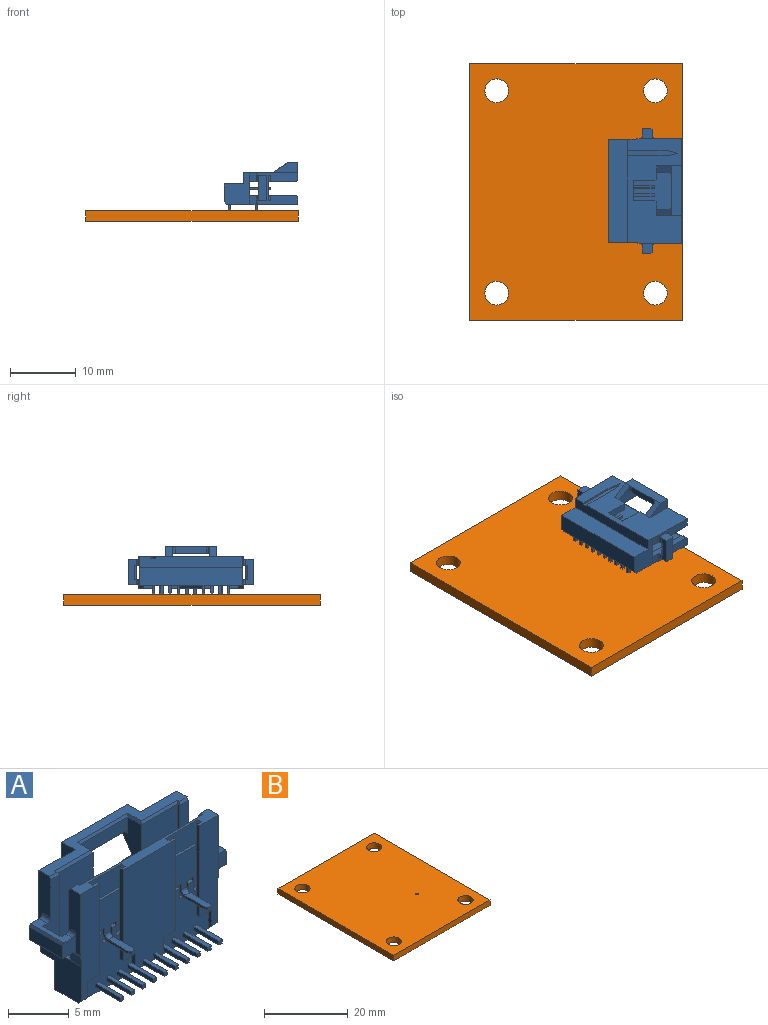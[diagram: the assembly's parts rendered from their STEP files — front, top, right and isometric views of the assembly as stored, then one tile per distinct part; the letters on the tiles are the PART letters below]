
ASSEMBLY  parts=2 mates=1
PART A: 290 faces, bbox 19.1x8.9x11.2 mm
  f0: plane 10.77x2.16mm, normal (0,-1,0), area 20.4mm2, adj f3,f26,f42,f44,f69,f72,f73,f155
  f1: plane 10.77x2.16mm, normal (0,-1,0), area 20.4mm2, adj f26,f28,f60,f62,f68,f70,f131,f132
  f2: plane 10.77x6.1mm, normal (0,-1,0), area 60.9mm2, adj f26,f71,f81,f82,f83,f104,f134,f135
  f3: plane 9.14x0.41mm, normal (1,0,0), area 3.7mm2, adj f0,f4,f15,f24,f26,f73,f74
  f4: plane 4.06x2.79mm, normal (0,-1,0), area 9.6mm2, adj f3,f5,f8,f11,f12,f13,f14,f19
  f5: cylinder r=0.38mm len=0.64mm, axis (1,0,0), area 0.4mm2, adj f4,f6,f8,f112
  f6: plane 2.57x0.64mm, normal (0,0,1), area 1.6mm2, adj f5,f8,f112,f113,f114,f115
  f7: plane 2.57x0.64mm, normal (0,0,1), area 1.6mm2, adj f106,f107,f109,f116,f117,f118
  f8: plane 2.94x1.24mm, normal (1,0,0), area 0.9mm2, adj f4,f5,f6,f9,f10,f11,f110,f115
  f9: cylinder r=0.64mm len=0.64mm, axis (1,0,0), area 0.6mm2, adj f8,f10,f110,f112
  f10: plane 4.06x3.4mm, normal (0,1,0), area 12mm2, adj f8,f9,f11,f12,f13,f14,f17,f18
  f11: plane 0.75x0.25mm, normal (0,0,-1), area 0.2mm2, adj f4,f8,f10,f13
  f12: plane 0.75x0.25mm, normal (0,0,-1), area 0.2mm2, adj f4,f10,f23,f112
  f13: plane 1.02x0.25mm, normal (-1,0,0), area 0.3mm2, adj f4,f10,f11,f14
  f14: plane 0.64x0.25mm, normal (0,0,-1), area 0.2mm2, adj f4,f10,f13,f16,f21
  f15: plane 6.32x0.36mm, normal (0,1,0), area 1mm2, adj f3,f17,f18,f19,f22,f24,f75,f76
  f16: plane 6.32x0.36mm, normal (0,1,0), area 1mm2, adj f14,f19,f20,f21,f80,f81,f84,f85
  f17: plane 3.81x0.25mm, normal (-1,0,0), area 1mm2, adj f10,f15,f18,f22
  f18: cylinder r=0.25mm len=0.25mm, axis (0,1,0), area 0.1mm2, adj f10,f15,f17,f19
  f19: plane 2.9x0.25mm, normal (0,0,1), area 0.7mm2, adj f4,f10,f15,f16,f18,f20
  f20: cylinder r=0.25mm len=0.25mm, axis (0,-1,0), area 0.1mm2, adj f10,f16,f19,f21
  f21: plane 3.81x0.25mm, normal (1,0,0), area 1mm2, adj f10,f14,f16,f20
  f22: plane 0.64x0.25mm, normal (0,0,-1), area 0.2mm2, adj f4,f10,f15,f17,f23
  f23: plane 1.02x0.25mm, normal (1,0,0), area 0.3mm2, adj f4,f10,f12,f22
  f24: plane 0.5x0.25mm, normal (0,0.87,0.5), area 0.1mm2, adj f3,f15,f26,f77
  f25: plane 16x2.72mm, normal (0,0,1), area 17.9mm2, adj f27,f29,f43,f148,f160,f161,f168,f169
  f26: plane 16x1.2mm, normal (0,0,1), area 10.7mm2, adj f0,f1,f2,f3,f24,f28,f35,f36
  f27: plane 1.02x0.25mm, normal (0,-0.87,0.5), area 0.3mm2, adj f25,f29,f55,f173
  f28: plane 6.17x1.35mm, normal (1,0,0), area 6.6mm2, adj f1,f26,f30,f31,f33,f35,f62
  f29: plane 6.17x1.35mm, normal (1,0,0), area 6.3mm2, adj f25,f27,f55,f57,f58,f59,f148
  f30: plane 2.11x1.52mm, normal (0,-1,0), area 2.4mm2, adj f28,f31,f32,f62,f63,f64,f65
  f31: cylinder r=0.38mm len=0.79mm, axis (0,1,0), area 0.5mm2, adj f28,f30,f32,f33
  f32: plane 3.86x1mm, normal (0,0,1), area 2.7mm2, adj f30,f31,f33,f55,f57,f58,f65,f67
  f33: plane 7.11x1.93mm, normal (0,1,0), area 8mm2, adj f28,f31,f32,f35,f37,f60,f62,f63
  f34: plane 7.11x1.93mm, normal (0,1,0), area 8mm2, adj f41,f42,f44,f45,f46,f47,f48,f49
  f35: plane 1.02x0.25mm, normal (0,0.87,0.5), area 0.3mm2, adj f26,f28,f33,f36
  f36: plane 0.4x0.25mm, normal (-0.87,0,0.5), area 0.1mm2, adj f26,f35,f37,f39
  f37: plane 7.11x0.25mm, normal (-1,0,0), area 1.8mm2, adj f33,f36,f38,f147
  f38: plane 13.97x7.11mm, normal (0,1,0), area 99.4mm2, adj f37,f39,f147,f191
  f39: plane 14.26x0.25mm, normal (0,0.87,0.5), area 4.1mm2, adj f26,f36,f38,f40
  f40: plane 0.4x0.25mm, normal (0.87,0,0.5), area 0.1mm2, adj f26,f39,f41,f191
  f41: plane 1.02x0.25mm, normal (0,0.87,0.5), area 0.3mm2, adj f26,f34,f40,f42
  f42: plane 6.17x1.35mm, normal (-1,0,0), area 6.6mm2, adj f0,f26,f34,f41,f44,f49,f50
  f43: plane 6.17x1.35mm, normal (-1,0,0), area 6.3mm2, adj f25,f53,f54,f56,f148,f159,f186
  f44: cylinder r=0.38mm len=1.35mm, axis (0,1,0), area 0.5mm2, adj f0,f34,f42,f45,f50,f157
  f45: plane 3.86x1.19mm, normal (0,0,-1), area 4mm2, adj f34,f44,f46,f50,f51,f53,f56,f159
  f46: cylinder r=0.33mm len=2.13mm, axis (0,1,0), area 1.5mm2, adj f34,f45,f47,f56
  f47: plane 2.13x1.03mm, normal (0.87,0,0.5), area 2.5mm2, adj f34,f46,f48,f56
  f48: plane 3.86x1mm, normal (0,0,1), area 2.7mm2, adj f34,f47,f49,f50,f52,f53,f54,f56
  f49: cylinder r=0.38mm len=0.79mm, axis (0,1,0), area 0.5mm2, adj f34,f42,f48,f50
  f50: plane 2.11x1.52mm, normal (0,-1,0), area 2.4mm2, adj f42,f44,f45,f48,f49,f51,f52
  f51: plane 3.86x1.27mm, normal (-1,0,0), area 4.9mm2, adj f45,f50,f52,f53
  f52: plane 3.86x0.25mm, normal (-0.87,0,0.5), area 1.1mm2, adj f48,f50,f51,f53
  f53: plane 2.11x1.52mm, normal (0,1,0), area 2.4mm2, adj f43,f45,f48,f51,f52,f54,f159
  f54: cylinder r=0.38mm len=0.94mm, axis (0,1,0), area 0.6mm2, adj f43,f48,f53,f56
  f55: plane 7.11x1.93mm, normal (0,-1,0), area 8mm2, adj f27,f29,f32,f57,f59,f61,f63,f66
  f56: plane 7.11x1.93mm, normal (0,-1,0), area 8mm2, adj f43,f45,f46,f47,f48,f54,f147,f158
  f57: cylinder r=0.38mm len=0.94mm, axis (0,1,0), area 0.6mm2, adj f29,f32,f55,f58
  f58: plane 2.11x1.52mm, normal (0,1,0), area 2.4mm2, adj f29,f32,f57,f59,f63,f64,f65
  f59: cylinder r=0.38mm len=1.35mm, axis (0,1,0), area 0.6mm2, adj f29,f55,f58,f61,f63,f148
  f60: plane 1.35x1.06mm, normal (0.99,0,-0.1), area 1.4mm2, adj f1,f33,f62,f68
  f61: plane 1.35x1.06mm, normal (0.99,0,-0.1), area 1.4mm2, adj f55,f59,f68,f148
  f62: cylinder r=0.38mm len=1.35mm, axis (0,1,0), area 0.5mm2, adj f1,f28,f30,f33,f60,f63
  f63: plane 3.86x1.19mm, normal (0,0,-1), area 4mm2, adj f30,f33,f55,f58,f59,f62,f64,f66
  f64: plane 3.86x1.27mm, normal (1,0,0), area 4.9mm2, adj f30,f58,f63,f65
  f65: plane 3.86x0.25mm, normal (0.87,0,0.5), area 1.1mm2, adj f30,f32,f58,f64
  f66: cylinder r=0.33mm len=2.13mm, axis (0,1,0), area 1.5mm2, adj f33,f55,f63,f67
  f67: plane 2.13x1.03mm, normal (-0.87,0,0.5), area 2.5mm2, adj f32,f33,f55,f66
  f68: plane 4.83x3.81mm, normal (1,0,0), area 13.4mm2, adj f1,f60,f61,f70,f93,f147,f148,f151
  f69: plane 0.64x0.41mm, normal (0,-0.71,-0.71), area 0.4mm2, adj f0,f72,f93,f155
  f70: plane 0.64x0.41mm, normal (0,-0.71,-0.71), area 0.4mm2, adj f1,f68,f93,f133
  f71: plane 3.35x0.41mm, normal (0,-0.71,-0.71), area 1.9mm2, adj f2,f83,f93,f135
  f72: plane 2.03x0.41mm, normal (1,0,0), area 0.7mm2, adj f0,f69,f73,f74
  f73: plane 1.37x0.41mm, normal (0,0,-1), area 0.6mm2, adj f0,f3,f72,f74
  f74: plane 5.61x5.54mm, normal (0,-1,0), area 18.9mm2, adj f3,f72,f73,f75,f81,f82,f83,f85
  f75: plane 0.7x0.3mm, normal (0,0,1), area 0.2mm2, adj f15,f74,f76,f78,f92
  f76: plane 6.32x0.3mm, normal (1,0,0), area 1.9mm2, adj f15,f75,f77,f78
  f77: plane 0.45x0.25mm, normal (0.87,0,0.5), area 0.1mm2, adj f24,f26,f76,f78
  f78: plane 6.58x3.8mm, normal (0,-1,0), area 22.1mm2, adj f26,f75,f76,f77,f79,f84,f85,f86
  f79: plane 0.45x0.25mm, normal (-0.87,0,0.5), area 0.1mm2, adj f26,f78,f80,f84
  f80: plane 0.5x0.25mm, normal (0,0.87,0.5), area 0.1mm2, adj f16,f26,f79,f81
  f81: plane 9.14x0.41mm, normal (-1,0,0), area 3.7mm2, adj f2,f4,f16,f26,f74,f80,f82
  f82: plane 1.37x0.41mm, normal (0,0,-1), area 0.6mm2, adj f2,f74,f81,f83
  f83: plane 2.03x0.41mm, normal (-1,0,0), area 0.7mm2, adj f2,f71,f74,f82
  f84: plane 6.32x0.3mm, normal (-1,0,0), area 1.9mm2, adj f16,f78,f79,f85
  f85: plane 0.7x0.3mm, normal (0,0,1), area 0.2mm2, adj f16,f74,f78,f84,f86
  f86: plane 1.02x0.3mm, normal (1,0,0), area 0.3mm2, adj f74,f78,f85,f87
  f87: plane 0.51x0.3mm, normal (0,0,1), area 0.2mm2, adj f74,f78,f86,f88
  f88: plane 1.02x0.3mm, normal (-1,0,0), area 0.3mm2, adj f74,f78,f87,f89
  f89: plane 1.09x0.3mm, normal (0,0,1), area 0.3mm2, adj f74,f78,f88,f90
  f90: plane 1.02x0.3mm, normal (1,0,0), area 0.3mm2, adj f74,f78,f89,f91
  f91: plane 0.51x0.3mm, normal (0,0,1), area 0.2mm2, adj f74,f78,f90,f92
  f92: plane 1.02x0.3mm, normal (-1,0,0), area 0.3mm2, adj f74,f75,f78,f91
  f93: plane 15.7x2.73mm, normal (0,0,-1), area 42.9mm2, adj f68,f69,f70,f71,f74,f94,f155,f156
  f94: plane 5.61x5.54mm, normal (0,-1,0), area 18.9mm2, adj f93,f95,f104,f131,f132,f133,f134,f135
  f95: plane 0.7x0.3mm, normal (0,0,1), area 0.2mm2, adj f94,f96,f100,f143,f144
  f96: plane 6.32x0.36mm, normal (0,1,0), area 1mm2, adj f95,f98,f124,f125,f126,f127,f131,f144
  f97: plane 6.32x0.36mm, normal (0,1,0), area 1mm2, adj f101,f103,f104,f127,f128,f129,f130,f136
  f98: plane 0.5x0.25mm, normal (0,0.87,0.5), area 0.1mm2, adj f26,f96,f99,f131
  f99: plane 0.45x0.25mm, normal (-0.87,0,0.5), area 0.1mm2, adj f26,f98,f100,f144
  f100: plane 6.58x3.8mm, normal (0,-1,0), area 22.1mm2, adj f26,f95,f99,f101,f102,f136,f137,f138
  f101: plane 6.32x0.3mm, normal (1,0,0), area 1.9mm2, adj f97,f100,f102,f136
  f102: plane 0.45x0.25mm, normal (0.87,0,0.5), area 0.1mm2, adj f26,f100,f101,f103
  f103: plane 0.5x0.25mm, normal (0,0.87,0.5), area 0.1mm2, adj f26,f97,f102,f104
  f104: plane 9.14x0.41mm, normal (1,0,0), area 3.7mm2, adj f2,f26,f94,f97,f103,f105,f134
  f105: plane 4.06x2.79mm, normal (0,-1,0), area 9.6mm2, adj f104,f106,f107,f109,f119,f120,f121,f123
  f106: cylinder r=0.38mm len=0.64mm, axis (1,0,0), area 0.4mm2, adj f7,f105,f107,f109
  f107: plane 2.94x1.24mm, normal (-1,0,0), area 0.9mm2, adj f7,f105,f106,f108,f111,f116,f119,f122
  f108: cylinder r=0.64mm len=0.64mm, axis (1,0,0), area 0.6mm2, adj f107,f109,f111,f122
  f109: plane 2.94x1.24mm, normal (1,0,0), area 0.9mm2, adj f7,f105,f106,f108,f111,f118,f120,f122
  f110: plane 2.57x0.64mm, normal (0,0,-1), area 1.6mm2, adj f8,f9,f112,f113,f114,f115
  f111: plane 2.57x0.64mm, normal (0,0,-1), area 1.6mm2, adj f107,f108,f109,f116,f117,f118
  f112: plane 2.94x1.24mm, normal (-1,0,0), area 0.9mm2, adj f4,f5,f6,f9,f10,f12,f110,f113
  f113: plane 0.26x0.25mm, normal (-0.87,-0.5,0), area 0.1mm2, adj f6,f110,f112,f114
  f114: plane 0.33x0.25mm, normal (0,-1,0), area 0.1mm2, adj f6,f110,f113,f115
  f115: plane 0.26x0.25mm, normal (0.87,-0.5,0), area 0.1mm2, adj f6,f8,f110,f114
  f116: plane 0.26x0.25mm, normal (-0.87,-0.5,0), area 0.1mm2, adj f7,f107,f111,f117
  f117: plane 0.33x0.25mm, normal (0,-1,0), area 0.1mm2, adj f7,f111,f116,f118
  f118: plane 0.26x0.25mm, normal (0.87,-0.5,0), area 0.1mm2, adj f7,f109,f111,f117
  f119: plane 0.75x0.25mm, normal (0,0,-1), area 0.2mm2, adj f105,f107,f121,f122
  f120: plane 0.75x0.25mm, normal (0,0,-1), area 0.2mm2, adj f105,f109,f122,f123
  f121: plane 1.02x0.25mm, normal (1,0,0), area 0.3mm2, adj f105,f119,f122,f130
  f122: plane 4.06x3.4mm, normal (0,1,0), area 12mm2, adj f107,f108,f109,f119,f120,f121,f123,f124
  f123: plane 1.02x0.25mm, normal (-1,0,0), area 0.3mm2, adj f105,f120,f122,f124
  f124: plane 0.64x0.25mm, normal (0,0,-1), area 0.2mm2, adj f96,f105,f122,f123,f125
  f125: plane 3.81x0.25mm, normal (1,0,0), area 1mm2, adj f96,f122,f124,f126
  f126: cylinder r=0.25mm len=0.25mm, axis (0,-1,0), area 0.1mm2, adj f96,f122,f125,f127
  f127: plane 2.9x0.25mm, normal (0,0,1), area 0.7mm2, adj f96,f97,f105,f122,f126,f128
  f128: cylinder r=0.25mm len=0.25mm, axis (0,1,0), area 0.1mm2, adj f97,f122,f127,f129
  f129: plane 3.81x0.25mm, normal (-1,0,0), area 1mm2, adj f97,f122,f128,f130
  f130: plane 0.64x0.25mm, normal (0,0,-1), area 0.2mm2, adj f97,f105,f121,f122,f129
  f131: plane 9.14x0.41mm, normal (-1,0,0), area 3.7mm2, adj f1,f26,f94,f96,f98,f105,f132
  f132: plane 1.37x0.41mm, normal (0,0,-1), area 0.6mm2, adj f1,f94,f131,f133
  f133: plane 2.03x0.41mm, normal (-1,0,0), area 0.7mm2, adj f1,f70,f94,f132
  f134: plane 1.37x0.41mm, normal (0,0,-1), area 0.6mm2, adj f2,f94,f104,f135
  f135: plane 2.03x0.41mm, normal (1,0,0), area 0.7mm2, adj f2,f71,f94,f134
  f136: plane 0.7x0.3mm, normal (0,0,1), area 0.2mm2, adj f94,f97,f100,f101,f137
  f137: plane 1.02x0.3mm, normal (-1,0,0), area 0.3mm2, adj f94,f100,f136,f138
  f138: plane 0.51x0.3mm, normal (0,0,1), area 0.2mm2, adj f94,f100,f137,f139
  f139: plane 1.02x0.3mm, normal (1,0,0), area 0.3mm2, adj f94,f100,f138,f140
  f140: plane 1.09x0.3mm, normal (0,0,1), area 0.3mm2, adj f94,f100,f139,f141
  f141: plane 1.02x0.3mm, normal (-1,0,0), area 0.3mm2, adj f94,f100,f140,f142
  f142: plane 0.51x0.3mm, normal (0,0,1), area 0.2mm2, adj f94,f100,f141,f143
  f143: plane 1.02x0.3mm, normal (1,0,0), area 0.3mm2, adj f94,f95,f100,f142
  f144: plane 6.32x0.3mm, normal (-1,0,0), area 1.9mm2, adj f95,f96,f99,f100
  f145: plane 3.18x0.38mm, normal (-1,0,0), area 1.2mm2, adj f147,f252,f253,f254
  f146: plane 2.95x0.38mm, normal (-1,0,0), area 1.1mm2, adj f94,f257,f258,f259
  f147: plane 15.7x3.73mm, normal (0,0,1), area 42.5mm2, adj f33,f34,f37,f38,f55,f56,f68,f145
  f148: plane 16x8.26mm, normal (0,1,0), area 86.4mm2, adj f25,f29,f43,f59,f61,f68,f147,f149
  f149: plane 1.42x0.38mm, normal (0.97,0,-0.26), area 0.4mm2, adj f148,f150,f152,f154
  f150: plane 6.2x0.25mm, normal (1,0,0), area 1.6mm2, adj f148,f149,f151,f152
  f151: plane 15.7x1.69mm, normal (0,0,-1), area 26.3mm2, adj f68,f148,f150,f152,f153,f155,f156
  f152: plane 7.62x0.76mm, normal (0,1,0), area 5.3mm2, adj f149,f150,f151,f153,f154
  f153: plane 6.2x0.25mm, normal (-1,0,0), area 1.6mm2, adj f148,f151,f152,f154
  f154: plane 1.42x0.38mm, normal (-0.97,0,-0.26), area 0.4mm2, adj f148,f149,f152,f153
  f155: plane 4.83x3.81mm, normal (-1,0,0), area 13.4mm2, adj f0,f69,f93,f147,f148,f151,f156,f157
  f156: plane 15.7x2.92mm, normal (0,1,0), area 45.9mm2, adj f68,f93,f151,f155
  f157: plane 1.35x1.06mm, normal (-0.99,0,-0.1), area 1.4mm2, adj f0,f34,f44,f155
  f158: plane 1.35x1.06mm, normal (-0.99,0,-0.1), area 1.4mm2, adj f56,f148,f155,f159
  f159: cylinder r=0.38mm len=1.35mm, axis (0,1,0), area 0.6mm2, adj f43,f45,f53,f56,f148,f158
  f160: plane 3.81x1.52mm, normal (1,0,0), area 4.1mm2, adj f25,f148,f161,f163
  f161: plane 7.62x1.52mm, normal (0,1,0), area 11.6mm2, adj f25,f160,f162,f163,f166,f190
  f162: plane 2.29x1.52mm, normal (0,0.83,-0.55), area 2.8mm2, adj f148,f161,f164,f165,f190
  f163: plane 2.29x1.52mm, normal (0,0.83,-0.55), area 2.8mm2, adj f148,f160,f161,f187,f188
  f164: plane 3.81x2.36mm, normal (1,0,0), area 5.9mm2, adj f162,f165,f167,f176,f178,f181,f183
  f165: cylinder r=0.38mm len=1.04mm, axis (0,-1,0), area 0.6mm2, adj f162,f164,f166,f167
  f166: plane 4.83x1.04mm, normal (0,0,-1), area 5mm2, adj f161,f165,f167,f188
  f167: plane 5.59x1.65mm, normal (0,-1,0), area 7.2mm2, adj f164,f165,f166,f168,f187,f188
  f168: plane 5.88x0.25mm, normal (0,-0.87,0.5), area 1.7mm2, adj f25,f167,f169,f183
  f169: plane 1.72x0.25mm, normal (-0.87,0,0.5), area 0.5mm2, adj f25,f168,f170,f187
  f170: plane 4.34x0.25mm, normal (0,-0.87,0.5), area 1.2mm2, adj f25,f169,f171,f173
  f171: plane 7.11x5.46mm, normal (0,-1,0), area 34mm2, adj f147,f170,f172,f174,f187,f189
  f172: plane 7.11x0.25mm, normal (-1,0,0), area 1.8mm2, adj f55,f147,f171,f173
  f173: plane 0.4x0.25mm, normal (-0.87,0,0.5), area 0.1mm2, adj f25,f27,f170,f172
  f174: plane 3.3x1.09mm, normal (-1,0,0), area 3.6mm2, adj f147,f148,f171,f175
  f175: plane 1.09x0.25mm, normal (-0.87,0,0.5), area 0.3mm2, adj f148,f174,f177,f189
  f176: plane 1.12x0.95mm, normal (0,0,1), area 1.1mm2, adj f148,f164,f178,f179
  f177: plane 1.12x0.95mm, normal (0,0,1), area 1.1mm2, adj f148,f175,f187,f189
  f178: plane 1.27x0.25mm, normal (0,-0.87,0.5), area 0.4mm2, adj f164,f176,f179,f181
  f179: plane 1.09x0.25mm, normal (0.87,0,0.5), area 0.3mm2, adj f148,f176,f178,f180
  f180: plane 3.3x1.09mm, normal (1,0,0), area 3.6mm2, adj f147,f148,f179,f181
  f181: plane 7.11x5.46mm, normal (0,-1,0), area 34mm2, adj f147,f164,f178,f180,f182,f185
  f182: plane 4.34x0.25mm, normal (0,-0.87,0.5), area 1.2mm2, adj f25,f181,f183,f184
  f183: plane 1.72x0.25mm, normal (0.87,0,0.5), area 0.5mm2, adj f25,f164,f168,f182
  f184: plane 0.4x0.25mm, normal (0.87,0,0.5), area 0.1mm2, adj f25,f182,f185,f186
  f185: plane 7.11x0.25mm, normal (1,0,0), area 1.8mm2, adj f56,f147,f181,f184
  f186: plane 1.02x0.25mm, normal (0,-0.87,0.5), area 0.3mm2, adj f25,f43,f56,f184
  f187: plane 3.81x2.36mm, normal (-1,0,0), area 5.9mm2, adj f163,f167,f169,f171,f177,f188,f189
  f188: cylinder r=0.38mm len=1.04mm, axis (0,-1,0), area 0.6mm2, adj f163,f166,f167,f187
  f189: plane 1.27x0.25mm, normal (0,-0.87,0.5), area 0.4mm2, adj f171,f175,f177,f187
  f190: plane 3.81x1.52mm, normal (-1,0,0), area 4.1mm2, adj f25,f148,f161,f162
  f191: plane 7.11x0.25mm, normal (1,0,0), area 1.8mm2, adj f34,f38,f40,f147
  f192: plane 3.18x0.38mm, normal (-1,0,0), area 1.2mm2, adj f147,f194,f197,f198
  f193: plane 2.95x0.38mm, normal (-1,0,0), area 1.1mm2, adj f74,f199,f200,f201
  f194: plane 3.18x0.38mm, normal (0,1,0), area 1.2mm2, adj f147,f192,f195,f198
  f195: plane 3.18x0.38mm, normal (1,0,0), area 1.2mm2, adj f147,f194,f197,f198
  f196: plane 2.95x0.38mm, normal (1,0,0), area 1.1mm2, adj f74,f199,f200,f201
  f197: plane 3.18x0.38mm, normal (0,-1,0), area 1.2mm2, adj f147,f192,f195,f198
  f198: plane 0.38x0.38mm, normal (0,0,1), area 0.1mm2, adj f192,f194,f195,f197
  f199: plane 2.95x0.38mm, normal (0,0,1), area 1.1mm2, adj f74,f193,f196,f200
  f200: plane 0.38x0.38mm, normal (0,-1,0), area 0.1mm2, adj f193,f196,f199,f201
  f201: plane 2.95x0.38mm, normal (0,0,-1), area 1.1mm2, adj f74,f193,f196,f200
  f202: plane 3.18x0.38mm, normal (-1,0,0), area 1.2mm2, adj f147,f204,f207,f208
  f203: plane 2.95x0.38mm, normal (-1,0,0), area 1.1mm2, adj f74,f209,f210,f211
  f204: plane 3.18x0.38mm, normal (0,1,0), area 1.2mm2, adj f147,f202,f205,f208
  f205: plane 3.18x0.38mm, normal (1,0,0), area 1.2mm2, adj f147,f204,f207,f208
  f206: plane 2.95x0.38mm, normal (1,0,0), area 1.1mm2, adj f74,f209,f210,f211
  f207: plane 3.18x0.38mm, normal (0,-1,0), area 1.2mm2, adj f147,f202,f205,f208
  f208: plane 0.38x0.38mm, normal (0,0,1), area 0.1mm2, adj f202,f204,f205,f207
  f209: plane 2.95x0.38mm, normal (0,0,1), area 1.1mm2, adj f74,f203,f206,f210
  f210: plane 0.38x0.38mm, normal (0,-1,0), area 0.1mm2, adj f203,f206,f209,f211
  f211: plane 2.95x0.38mm, normal (0,0,-1), area 1.1mm2, adj f74,f203,f206,f210
  f212: plane 3.18x0.38mm, normal (-1,0,0), area 1.2mm2, adj f147,f214,f217,f218
  f213: plane 2.95x0.38mm, normal (-1,0,0), area 1.1mm2, adj f74,f219,f220,f221
  f214: plane 3.18x0.38mm, normal (0,1,0), area 1.2mm2, adj f147,f212,f215,f218
  f215: plane 3.18x0.38mm, normal (1,0,0), area 1.2mm2, adj f147,f214,f217,f218
  f216: plane 2.95x0.38mm, normal (1,0,0), area 1.1mm2, adj f74,f219,f220,f221
  f217: plane 3.18x0.38mm, normal (0,-1,0), area 1.2mm2, adj f147,f212,f215,f218
  f218: plane 0.38x0.38mm, normal (0,0,1), area 0.1mm2, adj f212,f214,f215,f217
  f219: plane 2.95x0.38mm, normal (0,0,1), area 1.1mm2, adj f74,f213,f216,f220
  f220: plane 0.38x0.38mm, normal (0,-1,0), area 0.1mm2, adj f213,f216,f219,f221
  f221: plane 2.95x0.38mm, normal (0,0,-1), area 1.1mm2, adj f74,f213,f216,f220
  f222: plane 3.18x0.38mm, normal (-1,0,0), area 1.2mm2, adj f147,f224,f227,f228
  f223: plane 2.95x0.38mm, normal (-1,0,0), area 1.1mm2, adj f74,f229,f230,f231
  f224: plane 3.18x0.38mm, normal (0,1,0), area 1.2mm2, adj f147,f222,f225,f228
  f225: plane 3.18x0.38mm, normal (1,0,0), area 1.2mm2, adj f147,f224,f227,f228
  f226: plane 2.95x0.38mm, normal (1,0,0), area 1.1mm2, adj f74,f229,f230,f231
  f227: plane 3.18x0.38mm, normal (0,-1,0), area 1.2mm2, adj f147,f222,f225,f228
  f228: plane 0.38x0.38mm, normal (0,0,1), area 0.1mm2, adj f222,f224,f225,f227
  f229: plane 2.95x0.38mm, normal (0,0,1), area 1.1mm2, adj f74,f223,f226,f230
  f230: plane 0.38x0.38mm, normal (0,-1,0), area 0.1mm2, adj f223,f226,f229,f231
  f231: plane 2.95x0.38mm, normal (0,0,-1), area 1.1mm2, adj f74,f223,f226,f230
  f232: plane 3.18x0.38mm, normal (-1,0,0), area 1.2mm2, adj f147,f234,f237,f238
  f233: plane 2.54x0.38mm, normal (-1,0,0), area 1mm2, adj f2,f239,f240,f241
  f234: plane 3.18x0.38mm, normal (0,1,0), area 1.2mm2, adj f147,f232,f235,f238
  f235: plane 3.18x0.38mm, normal (1,0,0), area 1.2mm2, adj f147,f234,f237,f238
  f236: plane 2.54x0.38mm, normal (1,0,0), area 1mm2, adj f2,f239,f240,f241
  f237: plane 3.18x0.38mm, normal (0,-1,0), area 1.2mm2, adj f147,f232,f235,f238
  f238: plane 0.38x0.38mm, normal (0,0,1), area 0.1mm2, adj f232,f234,f235,f237
  f239: plane 2.54x0.38mm, normal (0,0,-1), area 1mm2, adj f2,f233,f236,f240
  f240: plane 0.38x0.38mm, normal (0,-1,0), area 0.1mm2, adj f233,f236,f239,f241
  f241: plane 2.54x0.38mm, normal (0,0,1), area 1mm2, adj f2,f233,f236,f240
  f242: plane 3.18x0.38mm, normal (-1,0,0), area 1.2mm2, adj f147,f244,f247,f248
  f243: plane 2.54x0.38mm, normal (-1,0,0), area 1mm2, adj f2,f249,f250,f251
  f244: plane 3.18x0.38mm, normal (0,1,0), area 1.2mm2, adj f147,f242,f245,f248
  f245: plane 3.18x0.38mm, normal (1,0,0), area 1.2mm2, adj f147,f244,f247,f248
  f246: plane 2.54x0.38mm, normal (1,0,0), area 1mm2, adj f2,f249,f250,f251
  f247: plane 3.18x0.38mm, normal (0,-1,0), area 1.2mm2, adj f147,f242,f245,f248
  f248: plane 0.38x0.38mm, normal (0,0,1), area 0.1mm2, adj f242,f244,f245,f247
  f249: plane 2.54x0.38mm, normal (0,0,-1), area 1mm2, adj f2,f243,f246,f250
  f250: plane 0.38x0.38mm, normal (0,-1,0), area 0.1mm2, adj f243,f246,f249,f251
  f251: plane 2.54x0.38mm, normal (0,0,1), area 1mm2, adj f2,f243,f246,f250
  f252: plane 3.18x0.38mm, normal (0,-1,0), area 1.2mm2, adj f145,f147,f253,f255
  f253: plane 0.38x0.38mm, normal (0,0,1), area 0.1mm2, adj f145,f252,f254,f255
  f254: plane 3.18x0.38mm, normal (0,1,0), area 1.2mm2, adj f145,f147,f253,f255
  f255: plane 3.18x0.38mm, normal (1,0,0), area 1.2mm2, adj f147,f252,f253,f254
  f256: plane 2.95x0.38mm, normal (1,0,0), area 1.1mm2, adj f94,f257,f258,f259
  f257: plane 2.95x0.38mm, normal (0,0,1), area 1.1mm2, adj f94,f146,f256,f258
  f258: plane 0.38x0.38mm, normal (0,-1,0), area 0.1mm2, adj f146,f256,f257,f259
  f259: plane 2.95x0.38mm, normal (0,0,-1), area 1.1mm2, adj f94,f146,f256,f258
  f260: plane 3.18x0.38mm, normal (-1,0,0), area 1.2mm2, adj f147,f262,f265,f266
  f261: plane 2.95x0.38mm, normal (-1,0,0), area 1.1mm2, adj f94,f267,f268,f269
  f262: plane 3.18x0.38mm, normal (0,1,0), area 1.2mm2, adj f147,f260,f263,f266
  f263: plane 3.18x0.38mm, normal (1,0,0), area 1.2mm2, adj f147,f262,f265,f266
  f264: plane 2.95x0.38mm, normal (1,0,0), area 1.1mm2, adj f94,f267,f268,f269
  f265: plane 3.18x0.38mm, normal (0,-1,0), area 1.2mm2, adj f147,f260,f263,f266
  f266: plane 0.38x0.38mm, normal (0,0,1), area 0.1mm2, adj f260,f262,f263,f265
  f267: plane 2.95x0.38mm, normal (0,0,1), area 1.1mm2, adj f94,f261,f264,f268
  f268: plane 0.38x0.38mm, normal (0,-1,0), area 0.1mm2, adj f261,f264,f267,f269
  f269: plane 2.95x0.38mm, normal (0,0,-1), area 1.1mm2, adj f94,f261,f264,f268
  f270: plane 3.18x0.38mm, normal (-1,0,0), area 1.2mm2, adj f147,f272,f275,f276
  f271: plane 2.95x0.38mm, normal (-1,0,0), area 1.1mm2, adj f94,f277,f278,f279
  f272: plane 3.18x0.38mm, normal (0,1,0), area 1.2mm2, adj f147,f270,f273,f276
  f273: plane 3.18x0.38mm, normal (1,0,0), area 1.2mm2, adj f147,f272,f275,f276
  f274: plane 2.95x0.38mm, normal (1,0,0), area 1.1mm2, adj f94,f277,f278,f279
  f275: plane 3.18x0.38mm, normal (0,-1,0), area 1.2mm2, adj f147,f270,f273,f276
  f276: plane 0.38x0.38mm, normal (0,0,1), area 0.1mm2, adj f270,f272,f273,f275
  f277: plane 2.95x0.38mm, normal (0,0,1), area 1.1mm2, adj f94,f271,f274,f278
  f278: plane 0.38x0.38mm, normal (0,-1,0), area 0.1mm2, adj f271,f274,f277,f279
  f279: plane 2.95x0.38mm, normal (0,0,-1), area 1.1mm2, adj f94,f271,f274,f278
  f280: plane 3.18x0.38mm, normal (-1,0,0), area 1.2mm2, adj f147,f282,f285,f286
  f281: plane 2.95x0.38mm, normal (-1,0,0), area 1.1mm2, adj f94,f287,f288,f289
  f282: plane 3.18x0.38mm, normal (0,1,0), area 1.2mm2, adj f147,f280,f283,f286
  f283: plane 3.18x0.38mm, normal (1,0,0), area 1.2mm2, adj f147,f282,f285,f286
  f284: plane 2.95x0.38mm, normal (1,0,0), area 1.1mm2, adj f94,f287,f288,f289
  f285: plane 3.18x0.38mm, normal (0,-1,0), area 1.2mm2, adj f147,f280,f283,f286
  f286: plane 0.38x0.38mm, normal (0,0,1), area 0.1mm2, adj f280,f282,f283,f285
  f287: plane 2.95x0.38mm, normal (0,0,1), area 1.1mm2, adj f94,f281,f284,f288
  f288: plane 0.38x0.38mm, normal (0,-1,0), area 0.1mm2, adj f281,f284,f287,f289
  f289: plane 2.95x0.38mm, normal (0,0,-1), area 1.1mm2, adj f94,f281,f284,f288
PART B: 11 faces, bbox 32.4x39.1x1.6 mm
  f0: plane 39.05x1.6mm, normal (-1,0,0), area 62.5mm2, adj f1,f7,f9,f10
  f1: plane 32.39x1.6mm, normal (0,-1,0), area 51.8mm2, adj f0,f2,f9,f10
  f2: plane 39.05x1.6mm, normal (1,0,0), area 62.5mm2, adj f1,f7,f9,f10
  f3: cylinder r=1.8mm len=3.6mm, axis (0,0,-1), area 18.1mm2, adj f9,f10
  f4: cylinder r=1.8mm len=3.6mm, axis (0,0,-1), area 18.1mm2, adj f9,f10
  f5: cylinder r=1.8mm len=3.6mm, axis (0,0,-1), area 18.1mm2, adj f9,f10
  f6: cylinder r=1.8mm len=3.6mm, axis (0,0,-1), area 18.1mm2, adj f9,f10
  f7: plane 32.39x1.6mm, normal (0,1,0), area 51.8mm2, adj f0,f2,f9,f10
  f8: cylinder r=0.35mm len=1.6mm, axis (0,0,-1), area 3.5mm2, adj f9,f10
  f9: plane 39.05x32.39mm, normal (0,0,1), area 1223.5mm2, adj f0,f1,f2,f3,f4,f5,f6,f7
  f10: plane 39.05x32.39mm, normal (0,0,-1), area 1223.5mm2, adj f0,f1,f2,f3,f4,f5,f6,f7
PLACE A rot(axis=(0.58,0.58,0.58),120deg) t=(32.27,19.68,4.95)mm
PLACE B at identity fixed
MATE fastened A.f200 <-> B.f8  axis (0,0,-1) through (21.91,13.97,0)mm
